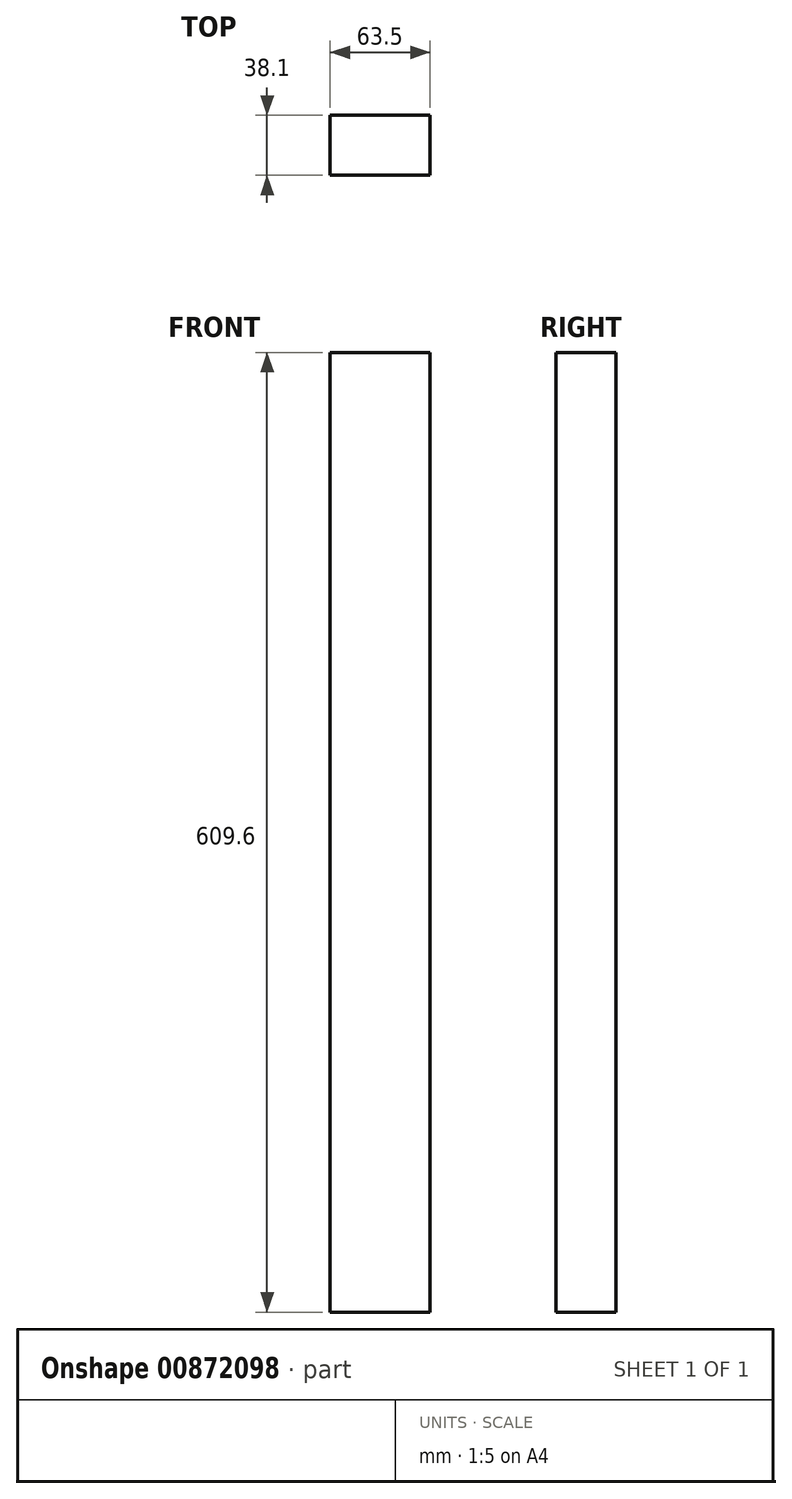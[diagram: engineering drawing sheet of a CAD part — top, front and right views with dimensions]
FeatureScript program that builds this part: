
annotation { "Feature Type Name" : "Feature", "Feature Type Description" : "" }
export const myFeature = defineFeature(function(context is Context, id is Id, definition is map)
    precondition{}
    {
        {
            var Q0;
            Q0=qCreatedBy(makeId("Front.planeOp"),FACE);
            var sketch = newSketch(context, id + "F0", { "sketchPlane" : qUnion([Q0])});
            skLineSegment(sketch, "E0.bottom", {"start": v(-3149.09, -1199.56) * mm, "end": v(-3212.59, -1199.56) * mm});
            skLineSegment(sketch, "E0.top", {"start": v(-3149.09, -589.96) * mm, "end": v(-3212.59, -589.96) * mm});
            skLineSegment(sketch, "E0.left", {"start": v(-3149.09, -1199.56) * mm, "end": v(-3149.09, -589.96) * mm});
            skLineSegment(sketch, "E0.right", {"start": v(-3212.59, -1199.56) * mm, "end": v(-3212.59, -589.96) * mm});
            skPoint(sketch, "E0.middle", {"position": v(-3180.84, -894.76) * mm});
            skSolve(sketch);
        }
        {
            var Q0;
            Q0=qSketchRegion(id+"F0",true);
            extrude(context, id + "F1", {"entities" : qUnion([Q0]), "depth" : 38.1 * mm, "offsetDistance" : 25.4 * mm});
        }
    });
